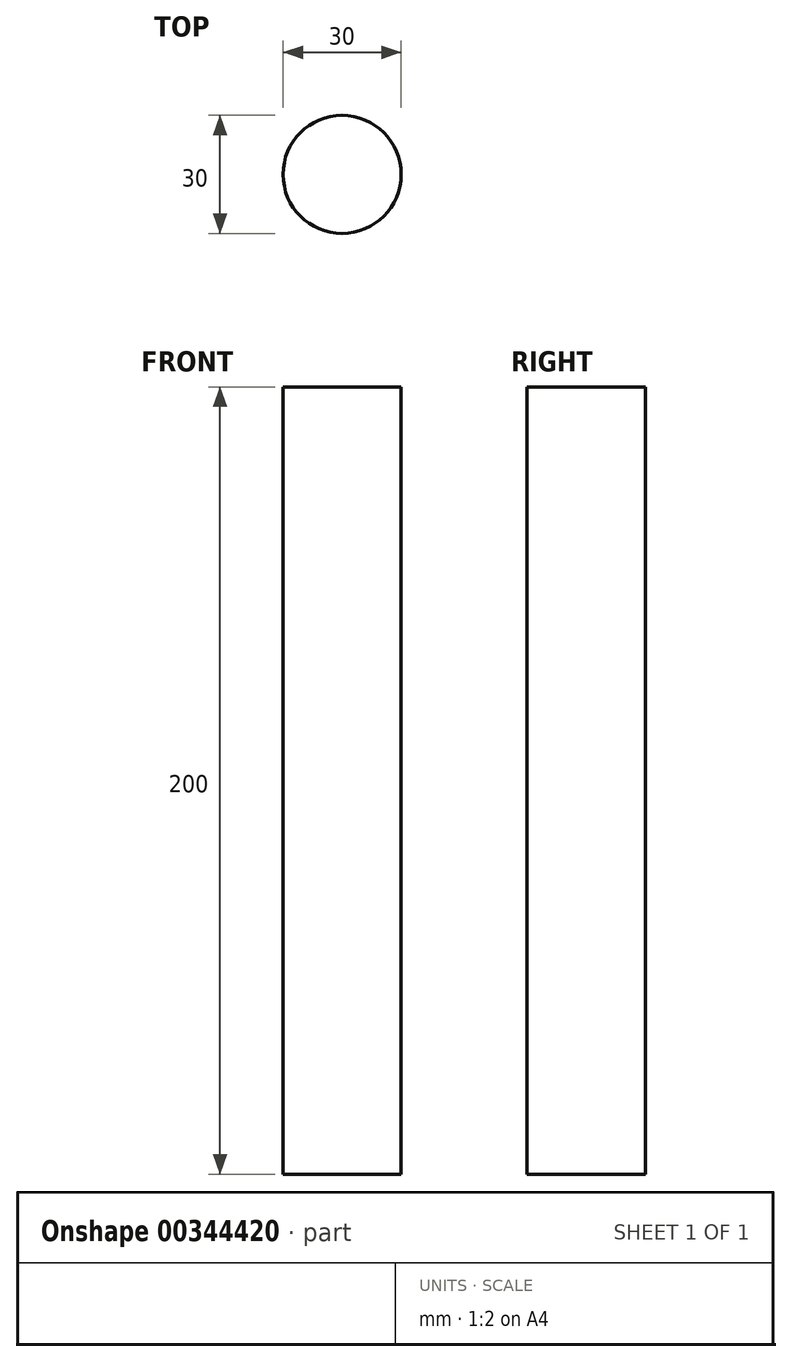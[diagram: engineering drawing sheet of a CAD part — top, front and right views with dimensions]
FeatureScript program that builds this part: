
annotation { "Feature Type Name" : "Feature", "Feature Type Description" : "" }
export const myFeature = defineFeature(function(context is Context, id is Id, definition is map)
    precondition{}
    {
        {
            var Q0;
            Q0=qCreatedBy(makeId("Top.planeOp"), FACE);
            var sketch = newSketch(context, id + "F0", { "sketchPlane" : qUnion([Q0])});
            skCircle(sketch, "E0", {"center": v(0, 0) * mm, "radius": 15 * mm});
            skSolve(sketch);
        }
        {
            var Q0;
            Q0 = qSketchRegion(id + "F0", true);
            extrude(context, id + "F1", {"entities" : qUnion([Q0]), "depth" : 200 * mm, "offsetDistance" : 25 * mm});
        }
    });
